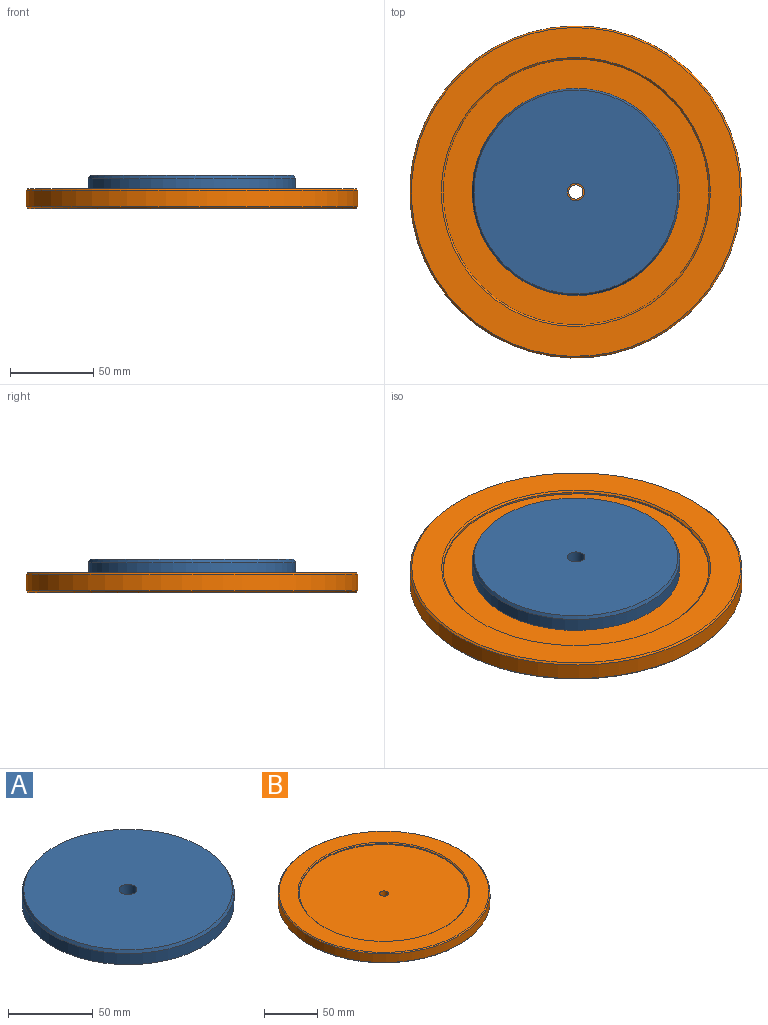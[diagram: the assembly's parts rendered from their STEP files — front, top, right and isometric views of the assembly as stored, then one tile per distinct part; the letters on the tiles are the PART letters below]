
ASSEMBLY  parts=2 mates=1
PART A: 5 faces, bbox 124.8x124.8x10 mm
  f0: cylinder r=62.4mm len=124.8mm, axis (0,0,-1), area 3136.6mm2, adj f2,f3
  f1: plane 122.8x122.8mm, normal (0,0,1), area 11757.1mm2, adj f3,f4
  f2: plane 124.8x124.8mm, normal (0,0,-1), area 12146mm2, adj f0,f4
  f3: cone r=61.4mm half-angle=26.6deg, axis (0,0,-1), area 869.7mm2, adj f0,f1
  f4: cylinder r=5.25mm len=10.5mm, axis (0,0,-1), area 329.9mm2, adj f1,f2
PART B: 9 faces, bbox 200x200x12 mm
  f0: cylinder r=100mm len=200mm, axis (0,0,-1), area 6283.2mm2, adj f5,f6
  f1: plane 198x198mm, normal (0,0,1), area 10178.8mm2, adj f6,f7
  f2: plane 198x198mm, normal (0,0,-1), area 30734mm2, adj f5,f8
  f3: cylinder r=80mm len=160mm, axis (0,0,1), area 502.7mm2, adj f4,f7
  f4: plane 160x160mm, normal (0,0,1), area 20049.4mm2, adj f3,f8
  f5: cone r=100mm half-angle=45deg, axis (0,0,1), area 884.1mm2, adj f0,f2
  f6: cone r=99mm half-angle=45deg, axis (0,0,-1), area 884.1mm2, adj f0,f1
  f7: cone r=80mm half-angle=45deg, axis (0,0,1), area 715.3mm2, adj f1,f3
  f8: cylinder r=4.25mm len=10mm, axis (0,0,1), area 267mm2, adj f2,f4
PLACE A t=(0.57,-0.46,2.82)mm
PLACE B t=(0.57,-0.46,-7.18)mm
MATE fastened A.f0 <-> B.f3  axis (0,0,-1) through (0.57,-0.46,2.82)mm
